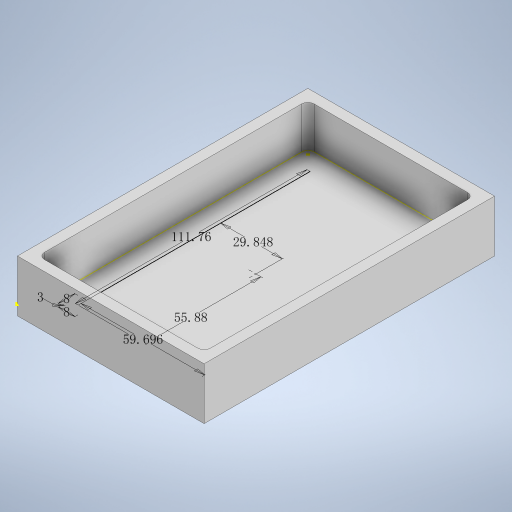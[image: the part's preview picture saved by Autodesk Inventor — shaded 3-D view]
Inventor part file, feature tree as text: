
AUTODESK INVENTOR PART (.ipt)
format: ipt  version: 2024 (Build 280153000, 153)  size: 264,192 bytes
history: native  units: mm
features: other x4, sketch x3, extrude x2, projected_geometry x2
ambient origin geometry x8: Origin, YZ Plane, XZ Plane, XY Plane, X Axis, Y Axis, Z Axis, Center Point
bodies: 实体1 (feature_tree)
feature tree (11):
  extrude  "拉伸1"  Depth=90.0mm
  extrude  "拉伸2"  Depth=80.0mm
  other  "面圆角1"
  other  "面圆角2"
  other  "面圆角3"
  other  "面圆角4"
  sketch  "草图4"  dims[d5=130.0mm d6=20.0mm d7=0.0mm d8=3.0mm d9=3.0mm d10=3.0mm d11=3.0mm d12=55.88mm d13=29.848mm d14=8.0mm d15=8.0mm d16=3.0mm d17=59.696mm d18=111.76mm]
  sketch  "草图1"  dims[d0=140.0mm d1=90.0mm]
  sketch  "草图2"  dims[d2=25.0mm d3=0.0mm d4=80.0mm]
  projected_geometry  "投影回路1"
  projected_geometry  "投影回路2"
